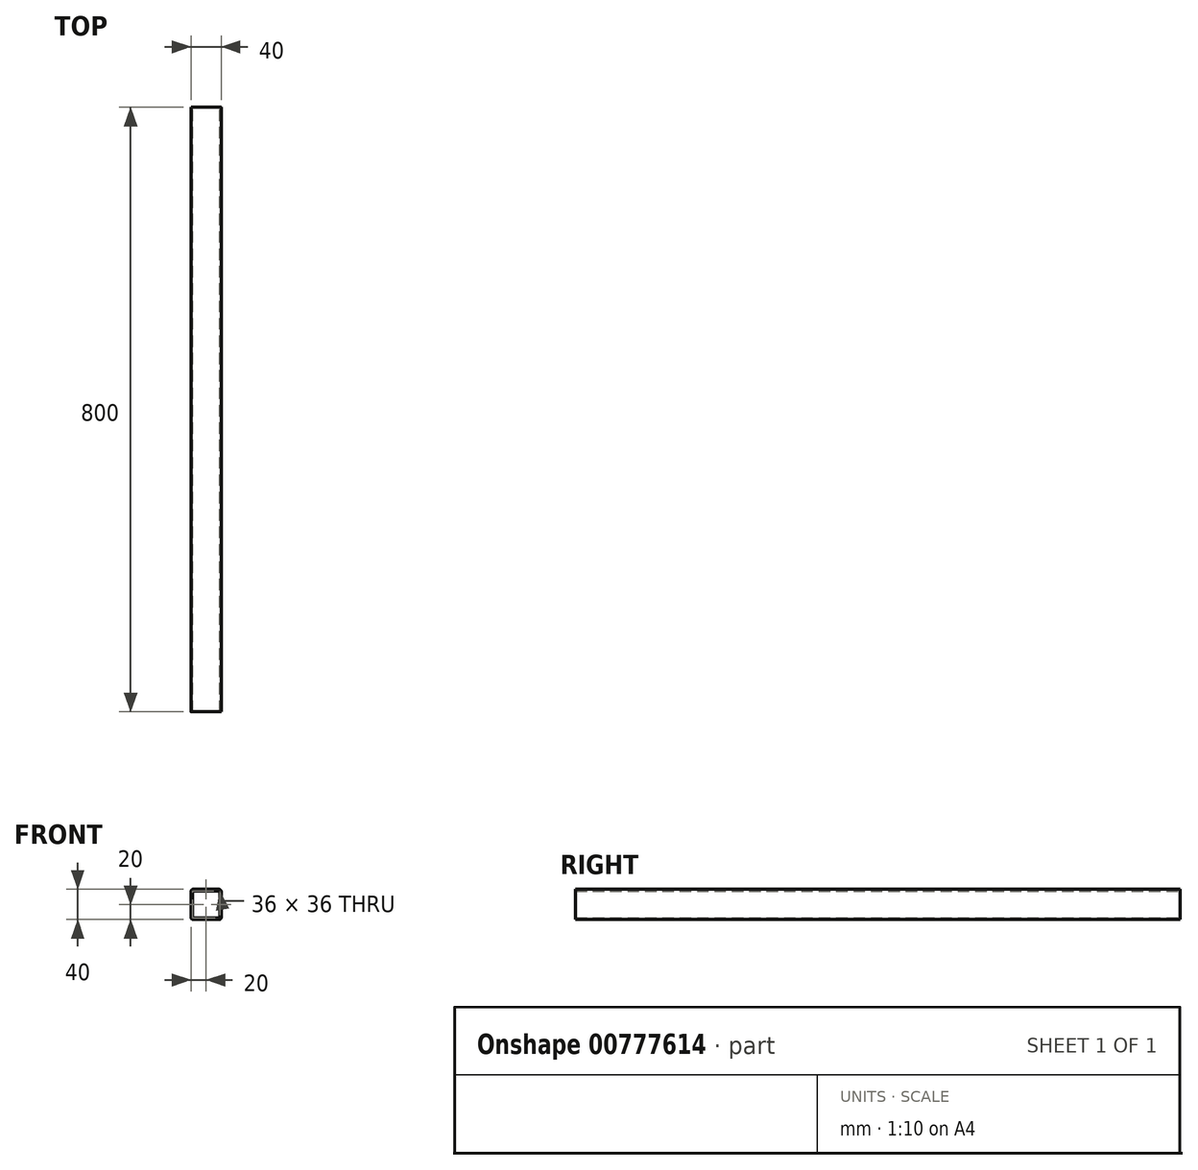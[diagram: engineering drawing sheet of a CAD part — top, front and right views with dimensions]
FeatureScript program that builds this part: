
annotation { "Feature Type Name" : "Feature", "Feature Type Description" : "" }
export const myFeature = defineFeature(function(context is Context, id is Id, definition is map)
    precondition{}
    {
        {
            var Q0;
            Q0=qCreatedBy(makeId("Front.planeOp"),FACE);
            var sketch = newSketch(context, id + "F0", { "sketchPlane" : qUnion([Q0])});
            skLineSegment(sketch, "E0.bottom", {"start": v(17, 20) * mm, "end": v(-17, 20) * mm});
            skLineSegment(sketch, "E0.top", {"start": v(17, -20) * mm, "end": v(-17, -20) * mm});
            skLineSegment(sketch, "E0.left", {"start": v(20, 17) * mm, "end": v(20, -17) * mm});
            skLineSegment(sketch, "E0.right", {"start": v(-20, 17) * mm, "end": v(-20, -17) * mm});
            skPoint(sketch, "E0.middle", {"position": v(0, 0) * mm});
            skPoint(sketch, "E1.visualSharp", {"position": v(-20, 20) * mm});
            skArc(sketch, "E1.filletArc", {"start": v(-17, 20) * mm, "mid": v(-19.12, 19.12) * mm, "end": v(-20, 17) * mm});
            skPoint(sketch, "E2.visualSharp", {"position": v(20, 20) * mm});
            skArc(sketch, "E2.filletArc", {"start": v(20, 17) * mm, "mid": v(19.12, 19.12) * mm, "end": v(17, 20) * mm});
            skPoint(sketch, "E3.visualSharp", {"position": v(20, -20) * mm});
            skArc(sketch, "E3.filletArc", {"start": v(17, -20) * mm, "mid": v(19.12, -19.12) * mm, "end": v(20, -17) * mm});
            skPoint(sketch, "E4.visualSharp", {"position": v(-20, -20) * mm});
            skArc(sketch, "E4.filletArc", {"start": v(-20, -17) * mm, "mid": v(-19.12, -19.12) * mm, "end": v(-17, -20) * mm});
            skLineSegment(sketch, "E5.0", {"start": v(18, 18) * mm, "end": v(-18, 18) * mm});
            skLineSegment(sketch, "E5.1", {"start": v(18, 18) * mm, "end": v(18, -18) * mm});
            skLineSegment(sketch, "E5.2", {"start": v(18, -18) * mm, "end": v(-18, -18) * mm});
            skLineSegment(sketch, "E5.3", {"start": v(-18, 18) * mm, "end": v(-18, -18) * mm});
            skSolve(sketch);
        }
        {
            var Q0;
            Q0=makeQuery(id+"F0.imprint","IMPRINT",FACE,{"disambiguationData":[TD([[makeQuery(id+"F0.imprint","IMPRINT",EDGE,{"derivedFrom":sQuery(id+"F0.wireOp",EDGE,"E0.bottom")}),1.0]])]});
            extrude(context, id + "F1", {"entities" : qUnion([Q0]), "endBound" : BoundingType.SYMMETRIC, "depth" : 800 * mm, "offsetDistance" : 25 * mm});
        }
    });
